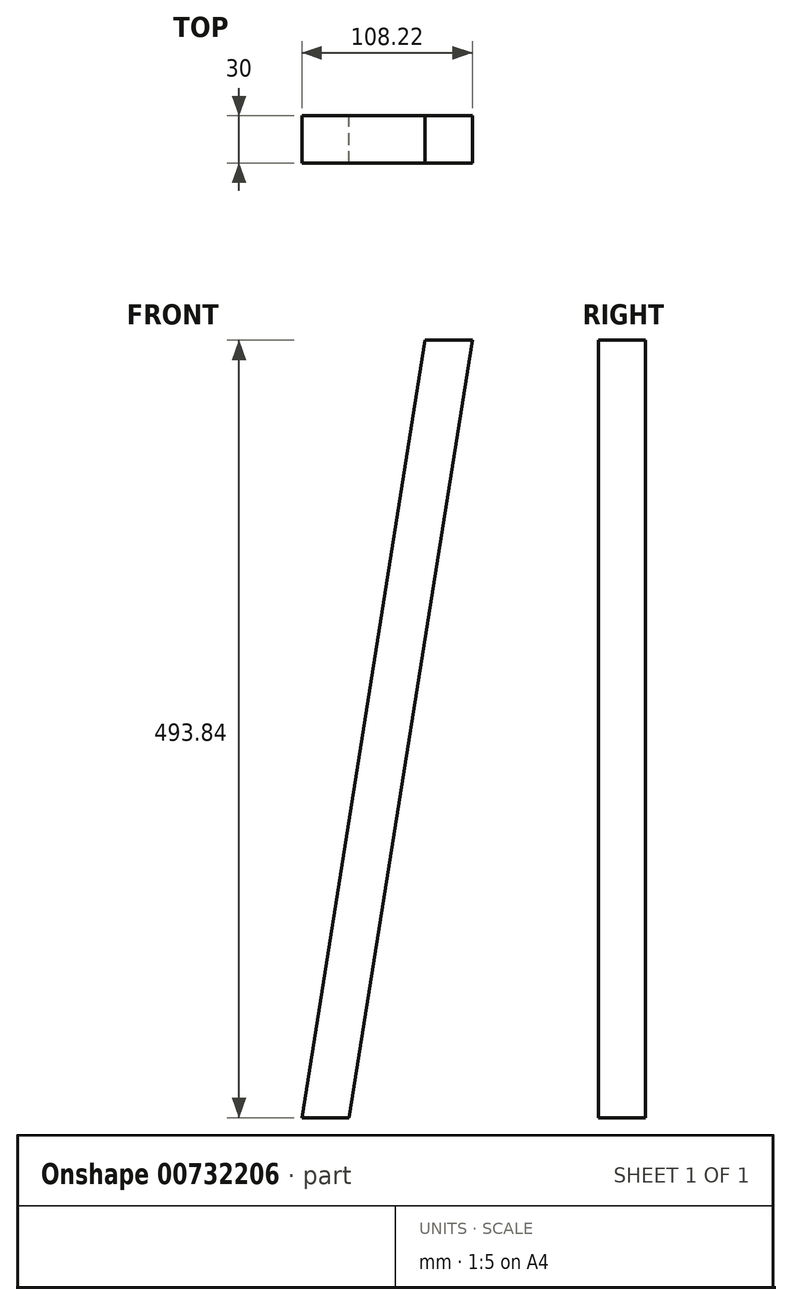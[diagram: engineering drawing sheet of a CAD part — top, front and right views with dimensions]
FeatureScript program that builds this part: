
annotation { "Feature Type Name" : "Feature", "Feature Type Description" : "" }
export const myFeature = defineFeature(function(context is Context, id is Id, definition is map)
    precondition{}
    {
        {
            var Q0;
            Q0=qCreatedBy(makeId("Front.planeOp"),FACE);
            var sketch = newSketch(context, id + "F0", { "sketchPlane" : qUnion([Q0])});
            skLineSegment(sketch, "E0", {"start": v(0, 0) * mm, "end": v(30, 0) * mm});
            skLineSegment(sketch, "E1", {"start": v(30, 0) * mm, "end": v(108.22, 493.84) * mm});
            skLineSegment(sketch, "E2", {"start": v(108.22, 493.84) * mm, "end": v(78.22, 493.84) * mm});
            skLineSegment(sketch, "E3", {"start": v(78.22, 493.84) * mm, "end": v(0, 0) * mm});
            skSolve(sketch);
        }
        {
            var Q0;
            Q0=makeQuery(id+"F0.imprint","IMPRINT",FACE,{"disambiguationData":[TD([[makeQuery(id+"F0.imprint","IMPRINT",EDGE,{"derivedFrom":sQuery(id+"F0.wireOp",EDGE,"E0")}),1.0]])]});
            extrude(context, id + "F1", {"entities" : qUnion([Q0]), "depth" : 30 * mm, "offsetDistance" : 25 * mm});
        }
    });
